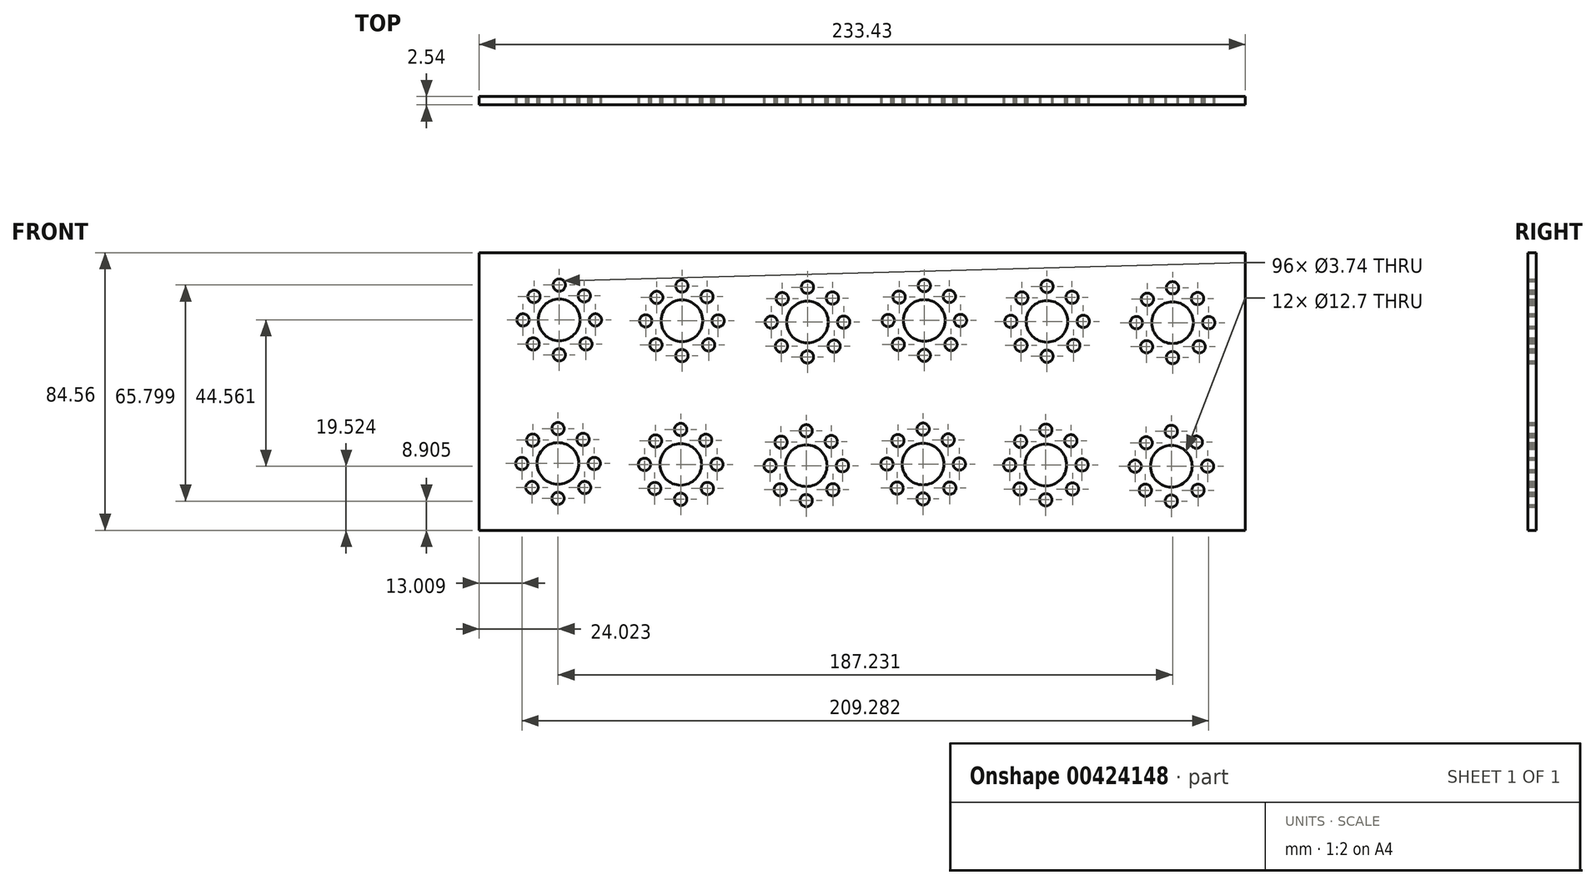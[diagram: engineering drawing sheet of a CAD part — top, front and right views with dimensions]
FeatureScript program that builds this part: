
annotation { "Feature Type Name" : "Feature", "Feature Type Description" : "" }
export const myFeature = defineFeature(function(context is Context, id is Id, definition is map)
    precondition{}
    {
        {
            var Q0;
            Q0=qCreatedBy(makeId("Front.planeOp"),FACE);
            var sketch = newSketch(context, id + "F0", { "sketchPlane" : qUnion([Q0])});
            skCircle(sketch, "E0", {"center": v(-103.99, 83.63) * mm, "radius": 6.35 * mm});
            skCircle(sketch, "E1", {"center": v(-103.99, 94.25) * mm, "radius": 1.87 * mm});
            skCircle(sketch, "E2", {"center": v(-103.99, 73.02) * mm, "radius": 1.87 * mm});
            skCircle(sketch, "E3", {"center": v(-92.95, 83.63) * mm, "radius": 1.87 * mm});
            skCircle(sketch, "E4", {"center": v(-115, 83.63) * mm, "radius": 1.87 * mm});
            skCircle(sketch, "E5", {"center": v(-111.9, 76.31) * mm, "radius": 1.87 * mm});
            skCircle(sketch, "E6", {"center": v(-96.36, 90.97) * mm, "radius": 1.87 * mm});
            skCircle(sketch, "E7", {"center": v(-95.85, 76.3) * mm, "radius": 1.87 * mm});
            skCircle(sketch, "E8", {"center": v(-111.66, 90.77) * mm, "radius": 1.87 * mm});
            skCircle(sketch, "E9", {"center": v(-66.6, 83.36) * mm, "radius": 6.35 * mm});
            skCircle(sketch, "E10", {"center": v(-66.6, 93.98) * mm, "radius": 1.87 * mm});
            skCircle(sketch, "E11", {"center": v(-66.6, 72.74) * mm, "radius": 1.87 * mm});
            skCircle(sketch, "E12", {"center": v(-55.57, 83.36) * mm, "radius": 1.87 * mm});
            skCircle(sketch, "E13", {"center": v(-77.62, 83.36) * mm, "radius": 1.87 * mm});
            skCircle(sketch, "E14", {"center": v(-74.51, 76.04) * mm, "radius": 1.87 * mm});
            skCircle(sketch, "E15", {"center": v(-58.97, 90.7) * mm, "radius": 1.87 * mm});
            skCircle(sketch, "E16", {"center": v(-58.47, 76.03) * mm, "radius": 1.87 * mm});
            skCircle(sketch, "E17", {"center": v(-74.27, 90.5) * mm, "radius": 1.87 * mm});
            skCircle(sketch, "E18", {"center": v(-28.36, 82.97) * mm, "radius": 6.35 * mm});
            skCircle(sketch, "E19", {"center": v(-28.36, 93.59) * mm, "radius": 1.87 * mm});
            skCircle(sketch, "E20", {"center": v(-28.36, 72.35) * mm, "radius": 1.87 * mm});
            skCircle(sketch, "E21", {"center": v(-17.32, 82.97) * mm, "radius": 1.87 * mm});
            skCircle(sketch, "E22", {"center": v(-39.37, 82.97) * mm, "radius": 1.87 * mm});
            skCircle(sketch, "E23", {"center": v(-36.27, 75.65) * mm, "radius": 1.87 * mm});
            skCircle(sketch, "E24", {"center": v(-20.73, 90.3) * mm, "radius": 1.87 * mm});
            skCircle(sketch, "E25", {"center": v(-20.22, 75.64) * mm, "radius": 1.87 * mm});
            skCircle(sketch, "E26", {"center": v(-36.03, 90.1) * mm, "radius": 1.87 * mm});
            skCircle(sketch, "E27", {"center": v(7.25, 83.47) * mm, "radius": 6.35 * mm});
            skCircle(sketch, "E28", {"center": v(7.25, 94.09) * mm, "radius": 1.87 * mm});
            skCircle(sketch, "E29", {"center": v(7.25, 72.85) * mm, "radius": 1.87 * mm});
            skCircle(sketch, "E30", {"center": v(18.28, 83.47) * mm, "radius": 1.87 * mm});
            skCircle(sketch, "E31", {"center": v(-3.77, 83.47) * mm, "radius": 1.87 * mm});
            skCircle(sketch, "E32", {"center": v(-0.67, 76.15) * mm, "radius": 1.87 * mm});
            skCircle(sketch, "E33", {"center": v(14.88, 90.8) * mm, "radius": 1.87 * mm});
            skCircle(sketch, "E34", {"center": v(15.38, 76.14) * mm, "radius": 1.87 * mm});
            skCircle(sketch, "E35", {"center": v(-0.43, 90.6) * mm, "radius": 1.87 * mm});
            skCircle(sketch, "E36", {"center": v(44.63, 83.2) * mm, "radius": 6.35 * mm});
            skCircle(sketch, "E37", {"center": v(44.63, 93.81) * mm, "radius": 1.87 * mm});
            skCircle(sketch, "E38", {"center": v(44.63, 72.57) * mm, "radius": 1.87 * mm});
            skCircle(sketch, "E39", {"center": v(55.67, 83.2) * mm, "radius": 1.87 * mm});
            skCircle(sketch, "E40", {"center": v(33.62, 83.2) * mm, "radius": 1.87 * mm});
            skCircle(sketch, "E41", {"center": v(36.72, 75.87) * mm, "radius": 1.87 * mm});
            skCircle(sketch, "E42", {"center": v(52.26, 90.53) * mm, "radius": 1.87 * mm});
            skCircle(sketch, "E43", {"center": v(52.77, 75.86) * mm, "radius": 1.87 * mm});
            skCircle(sketch, "E44", {"center": v(36.96, 90.32) * mm, "radius": 1.87 * mm});
            skCircle(sketch, "E45", {"center": v(82.87, 82.8) * mm, "radius": 6.35 * mm});
            skCircle(sketch, "E46", {"center": v(82.87, 93.42) * mm, "radius": 1.87 * mm});
            skCircle(sketch, "E47", {"center": v(82.87, 72.18) * mm, "radius": 1.87 * mm});
            skCircle(sketch, "E48", {"center": v(93.91, 82.8) * mm, "radius": 1.87 * mm});
            skCircle(sketch, "E49", {"center": v(71.86, 82.8) * mm, "radius": 1.87 * mm});
            skCircle(sketch, "E50", {"center": v(74.96, 75.48) * mm, "radius": 1.87 * mm});
            skCircle(sketch, "E51", {"center": v(90.5, 90.14) * mm, "radius": 1.87 * mm});
            skCircle(sketch, "E52", {"center": v(91, 75.47) * mm, "radius": 1.87 * mm});
            skCircle(sketch, "E53", {"center": v(75.2, 89.93) * mm, "radius": 1.87 * mm});
            skLineSegment(sketch, "E54.bottom", {"start": v(-128.38, 104.11) * mm, "end": v(105.05, 104.11) * mm});
            skLineSegment(sketch, "E54.top", {"start": v(-128.38, 19.55) * mm, "end": v(105.05, 19.55) * mm});
            skLineSegment(sketch, "E54.left", {"start": v(-128.38, 104.11) * mm, "end": v(-128.38, 19.55) * mm});
            skLineSegment(sketch, "E54.right", {"start": v(105.05, 104.11) * mm, "end": v(105.05, 19.55) * mm});
            skCircle(sketch, "E55", {"center": v(-104.36, 39.9) * mm, "radius": 6.35 * mm});
            skCircle(sketch, "E56", {"center": v(-104.36, 50.52) * mm, "radius": 1.87 * mm});
            skCircle(sketch, "E57", {"center": v(-104.36, 29.29) * mm, "radius": 1.87 * mm});
            skCircle(sketch, "E58", {"center": v(-93.32, 39.9) * mm, "radius": 1.87 * mm});
            skCircle(sketch, "E59", {"center": v(-115.37, 39.9) * mm, "radius": 1.87 * mm});
            skCircle(sketch, "E60", {"center": v(-112.27, 32.58) * mm, "radius": 1.87 * mm});
            skCircle(sketch, "E61", {"center": v(-96.72, 47.24) * mm, "radius": 1.87 * mm});
            skCircle(sketch, "E62", {"center": v(-96.22, 32.57) * mm, "radius": 1.87 * mm});
            skCircle(sketch, "E63", {"center": v(-112.03, 47.04) * mm, "radius": 1.87 * mm});
            skCircle(sketch, "E64", {"center": v(-66.97, 39.63) * mm, "radius": 6.35 * mm});
            skCircle(sketch, "E65", {"center": v(-66.97, 50.25) * mm, "radius": 1.87 * mm});
            skCircle(sketch, "E66", {"center": v(-66.97, 29.01) * mm, "radius": 1.87 * mm});
            skCircle(sketch, "E67", {"center": v(-55.94, 39.63) * mm, "radius": 1.87 * mm});
            skCircle(sketch, "E68", {"center": v(-77.99, 39.63) * mm, "radius": 1.87 * mm});
            skCircle(sketch, "E69", {"center": v(-74.88, 32.3) * mm, "radius": 1.87 * mm});
            skCircle(sketch, "E70", {"center": v(-59.34, 46.97) * mm, "radius": 1.87 * mm});
            skCircle(sketch, "E71", {"center": v(-58.84, 32.3) * mm, "radius": 1.87 * mm});
            skCircle(sketch, "E72", {"center": v(-74.64, 46.76) * mm, "radius": 1.87 * mm});
            skCircle(sketch, "E73", {"center": v(-28.73, 39.24) * mm, "radius": 6.35 * mm});
            skCircle(sketch, "E74", {"center": v(-28.73, 49.86) * mm, "radius": 1.87 * mm});
            skCircle(sketch, "E75", {"center": v(-28.73, 28.62) * mm, "radius": 1.87 * mm});
            skCircle(sketch, "E76", {"center": v(-17.7, 39.24) * mm, "radius": 1.87 * mm});
            skCircle(sketch, "E77", {"center": v(-39.74, 39.24) * mm, "radius": 1.87 * mm});
            skCircle(sketch, "E78", {"center": v(-36.64, 31.92) * mm, "radius": 1.87 * mm});
            skCircle(sketch, "E79", {"center": v(-21.1, 46.58) * mm, "radius": 1.87 * mm});
            skCircle(sketch, "E80", {"center": v(-20.6, 31.9) * mm, "radius": 1.87 * mm});
            skCircle(sketch, "E81", {"center": v(-36.4, 46.37) * mm, "radius": 1.87 * mm});
            skCircle(sketch, "E82", {"center": v(6.88, 39.74) * mm, "radius": 6.35 * mm});
            skCircle(sketch, "E83", {"center": v(6.88, 50.36) * mm, "radius": 1.87 * mm});
            skCircle(sketch, "E84", {"center": v(6.88, 29.12) * mm, "radius": 1.87 * mm});
            skCircle(sketch, "E85", {"center": v(17.91, 39.74) * mm, "radius": 1.87 * mm});
            skCircle(sketch, "E86", {"center": v(-4.14, 39.74) * mm, "radius": 1.87 * mm});
            skCircle(sketch, "E87", {"center": v(-1.04, 32.42) * mm, "radius": 1.87 * mm});
            skCircle(sketch, "E88", {"center": v(14.5, 47.08) * mm, "radius": 1.87 * mm});
            skCircle(sketch, "E89", {"center": v(15.01, 32.4) * mm, "radius": 1.87 * mm});
            skCircle(sketch, "E90", {"center": v(-0.8, 46.87) * mm, "radius": 1.87 * mm});
            skCircle(sketch, "E91", {"center": v(44.26, 39.46) * mm, "radius": 6.35 * mm});
            skCircle(sketch, "E92", {"center": v(44.26, 50.08) * mm, "radius": 1.87 * mm});
            skCircle(sketch, "E93", {"center": v(44.26, 28.84) * mm, "radius": 1.87 * mm});
            skCircle(sketch, "E94", {"center": v(55.3, 39.46) * mm, "radius": 1.87 * mm});
            skCircle(sketch, "E95", {"center": v(33.25, 39.46) * mm, "radius": 1.87 * mm});
            skCircle(sketch, "E96", {"center": v(36.35, 32.14) * mm, "radius": 1.87 * mm});
            skCircle(sketch, "E97", {"center": v(51.9, 46.8) * mm, "radius": 1.87 * mm});
            skCircle(sketch, "E98", {"center": v(52.4, 32.13) * mm, "radius": 1.87 * mm});
            skCircle(sketch, "E99", {"center": v(36.6, 46.6) * mm, "radius": 1.87 * mm});
            skCircle(sketch, "E100", {"center": v(82.5, 39.07) * mm, "radius": 6.35 * mm});
            skCircle(sketch, "E101", {"center": v(82.5, 49.7) * mm, "radius": 1.87 * mm});
            skCircle(sketch, "E102", {"center": v(82.5, 28.45) * mm, "radius": 1.87 * mm});
            skCircle(sketch, "E103", {"center": v(93.54, 39.07) * mm, "radius": 1.87 * mm});
            skCircle(sketch, "E104", {"center": v(71.5, 39.07) * mm, "radius": 1.87 * mm});
            skCircle(sketch, "E105", {"center": v(74.6, 31.75) * mm, "radius": 1.87 * mm});
            skCircle(sketch, "E106", {"center": v(90.14, 46.41) * mm, "radius": 1.87 * mm});
            skCircle(sketch, "E107", {"center": v(90.64, 31.74) * mm, "radius": 1.87 * mm});
            skCircle(sketch, "E108", {"center": v(74.83, 46.2) * mm, "radius": 1.87 * mm});
            skSolve(sketch);
        }
        {
            var Q0;
            Q0 = qSketchRegion(id + "F0", true);
            var Q1;
            Q1=makeQuery(id+"F0.imprint","IMPRINT",FACE,{"disambiguationData":[TD([[makeQuery(id+"F0.imprint","IMPRINT",EDGE,{"derivedFrom":sQuery(id+"F0.wireOp",EDGE,"RMUyz42M-Bwck-izP0-UmXt-mctbMuAU1B3g.bottom")}),1.0]])]});
            extrude(context, id + "F1", {"entities" : qUnion([Q0, Q1]), "depth" : 2.54 * mm});
        }
    });
